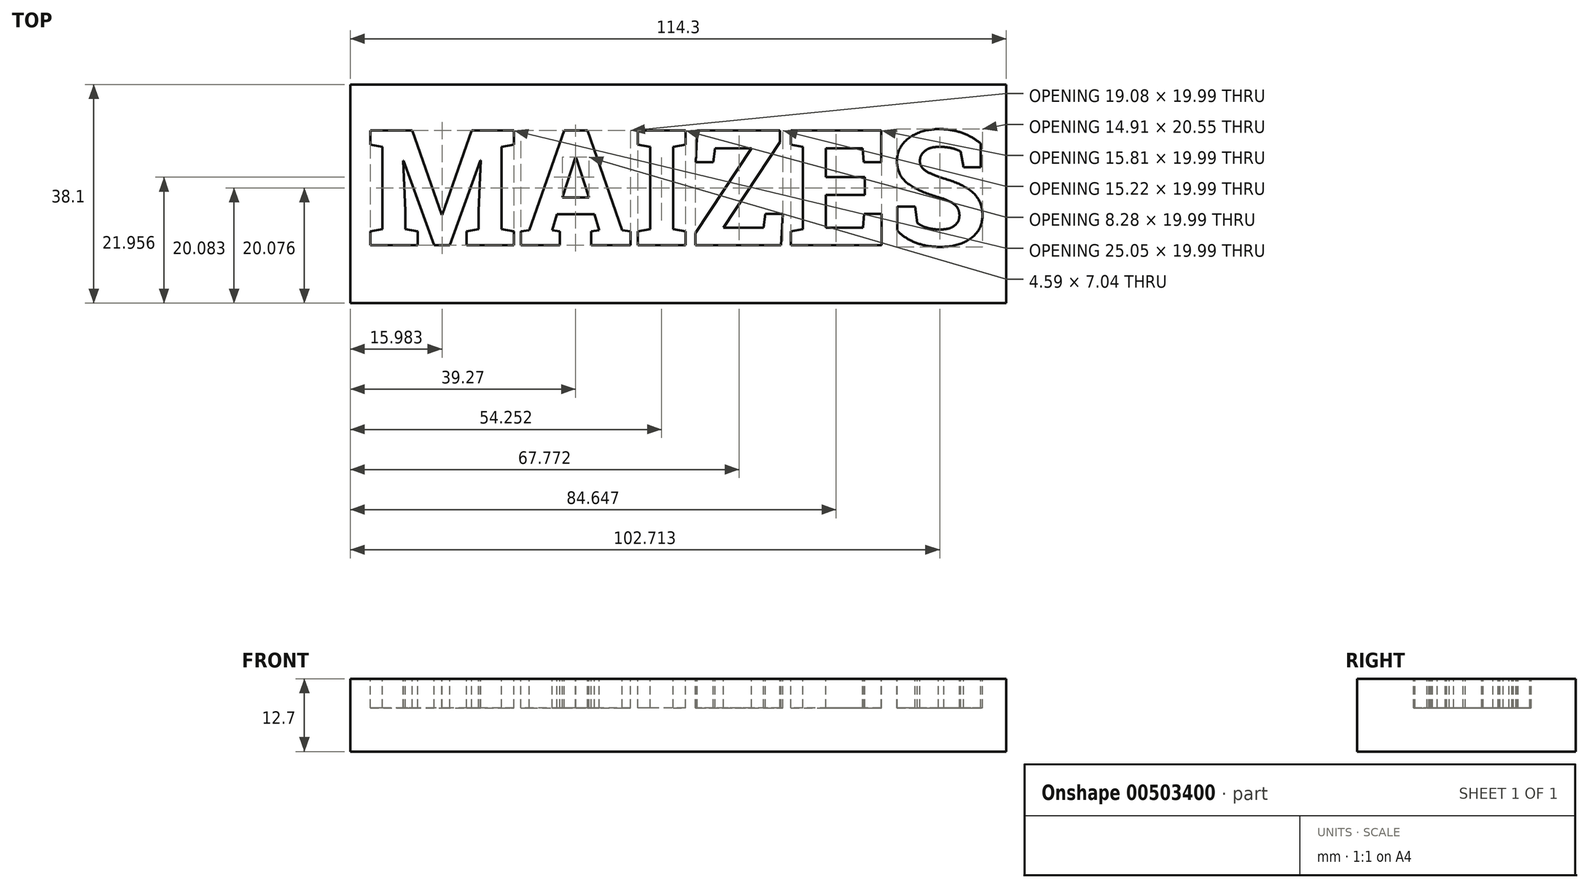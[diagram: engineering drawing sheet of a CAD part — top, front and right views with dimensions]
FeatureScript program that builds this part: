
annotation { "Feature Type Name" : "Feature", "Feature Type Description" : "" }
export const myFeature = defineFeature(function(context is Context, id is Id, definition is map)
    precondition{}
    {
        {
            var Q0;
            Q0=qCreatedBy(makeId("Top.planeOp"),FACE);
            var sketch = newSketch(context, id + "F0", { "sketchPlane" : qUnion([Q0])});
            skLineSegment(sketch, "E0.bottom", {"start": v(-57.24, 19.2) * mm, "end": v(57.06, 19.2) * mm});
            skLineSegment(sketch, "E0.top", {"start": v(-57.24, -18.9) * mm, "end": v(57.06, -18.9) * mm});
            skLineSegment(sketch, "E0.left", {"start": v(-57.24, 19.2) * mm, "end": v(-57.24, -18.9) * mm});
            skLineSegment(sketch, "E0.right", {"start": v(57.06, 19.2) * mm, "end": v(57.06, -18.9) * mm});
            skSolve(sketch);
        }
        {
            var Q0;
            Q0 = qSketchRegion(id + "F0", true);
            extrude(context, id + "F1", {"entities" : qUnion([Q0]), "depth" : 12.7 * mm});
        }
        {
            var Q0;
            Q0=makeQuery(id+"F1.opExtrude","CAP_FACE",FACE,{"disambiguationData":[OSD([sQuery(id+"F0.wireOp",EDGE,"E0.bottom"),sQuery(id+"F0.wireOp",EDGE,"E0.top"),sQuery(id+"F0.wireOp",EDGE,"E0.left"),sQuery(id+"F0.wireOp",EDGE,"E0.right")])],"isStart":false});
            var sketch = newSketch(context, id + "F2", { "sketchPlane" : qUnion([Q0])});
            skText(sketch, "E1", { "text": "MAIZES", "fontName": "RobotoSlab-Bold.ttf"});
            const initialGuessF2  = {"E1": [-0.05455, -0.0088, 1, 0, 0.02024]};
            skSetInitialGuess(sketch, initialGuessF2);
            skSolve(sketch);
        }
        {
            var Q0;
            Q0 = qSketchRegion(id + "F2", true);
            extrude(context, id + "F3", {"entities" : qUnion([Q0]), "operationType" : NewBodyOperationType.REMOVE, "oppositeDirection" : true, "depth" : 5.08 * mm});
        }
    });
